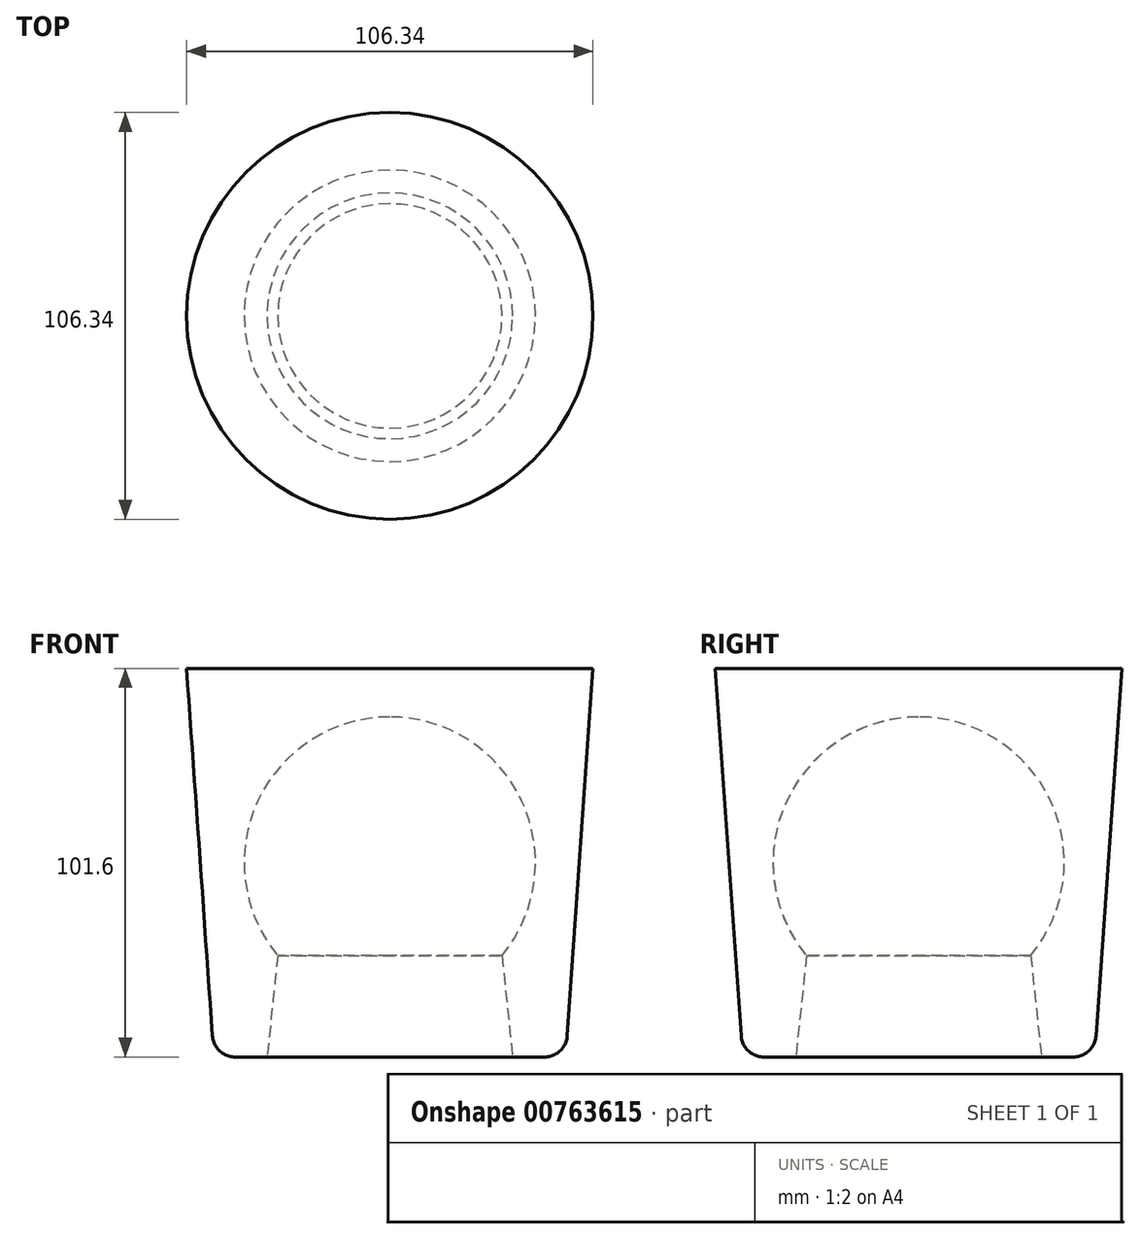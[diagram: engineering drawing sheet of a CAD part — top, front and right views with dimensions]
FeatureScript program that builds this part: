
annotation { "Feature Type Name" : "Feature", "Feature Type Description" : "" }
export const myFeature = defineFeature(function(context is Context, id is Id, definition is map)
    precondition{}
    {
        {
            var Q0;
            Q0=qCreatedBy(makeId("Right.planeOp"),FACE);
            var sketch = newSketch(context, id + "F0", { "sketchPlane" : qUnion([Q0])});
            skLineSegment(sketch, "E0", {"start": v(0, 0) * mm, "end": v(0, 88.9) * mm, "construction": true});
            skArc(sketch, "E1", {"start": v(0, 88.9) * mm, "mid": v(-34.48, 67) * mm, "end": v(-29.34, 26.5) * mm});
            skLineSegment(sketch, "E2", {"start": v(-32.13, 0) * mm, "end": v(-29.34, 26.5) * mm});
            skLineSegment(sketch, "E3", {"start": v(-32.13, 0) * mm, "end": v(0, 0) * mm});
            skLineSegment(sketch, "E4", {"start": v(0, 0) * mm, "end": v(0, -82) * mm, "construction": true});
            skLineSegment(sketch, "E5", {"start": v(0, -82) * mm, "end": v(0, -82) * mm});
            skLineSegment(sketch, "E6", {"start": v(-40.77, -82) * mm, "end": v(0, -82) * mm, "construction": true});
            skLineSegment(sketch, "E7", {"start": v(-32.13, 0) * mm, "end": v(-40.77, -82) * mm, "construction": true});
            skLineSegment(sketch, "E8", {"start": v(0, 0) * mm, "end": v(-40.47, 0) * mm});
            skArc(sketch, "E9", {"start": v(-40.47, 0) * mm, "mid": v(-44.54, 1.6) * mm, "end": v(-46.42, 5.54) * mm});
            skLineSegment(sketch, "E10", {"start": v(-46.42, 5.54) * mm, "end": v(-53.17, 101.6) * mm});
            skLineSegment(sketch, "E11", {"start": v(-53.17, 101.6) * mm, "end": v(-54.39, 118.95) * mm, "construction": true});
            skLineSegment(sketch, "E12", {"start": v(-53.17, 101.6) * mm, "end": v(0, 101.6) * mm});
            skLineSegment(sketch, "E13", {"start": v(0, 101.6) * mm, "end": v(0, 101.6) * mm});
            skLineSegment(sketch, "E14", {"start": v(0, 88.9) * mm, "end": v(0, 101.6) * mm});
            skSolve(sketch);
        }
        {
            var Q0;
            Q0=makeQuery(id+"F0.imprint","IMPRINT",FACE,{"disambiguationData":[TD([[makeQuery(id+"F0.imprint","IMPRINT",EDGE,{"derivedFrom":sQuery(id+"F0.wireOp",EDGE,"E1")}),-1.0]])]});
            var Q1;
            Q1=sQuery(id+"F0.wireOp",EDGE,"E0");
            revolve(context, id + "F1", {"surfaceOperationType" : NewSurfaceOperationType.NEW, "entities" : qUnion([Q0]), "axis" : qUnion([Q1]), "revolveType" : RevolveType.FULL});
        }
    });
